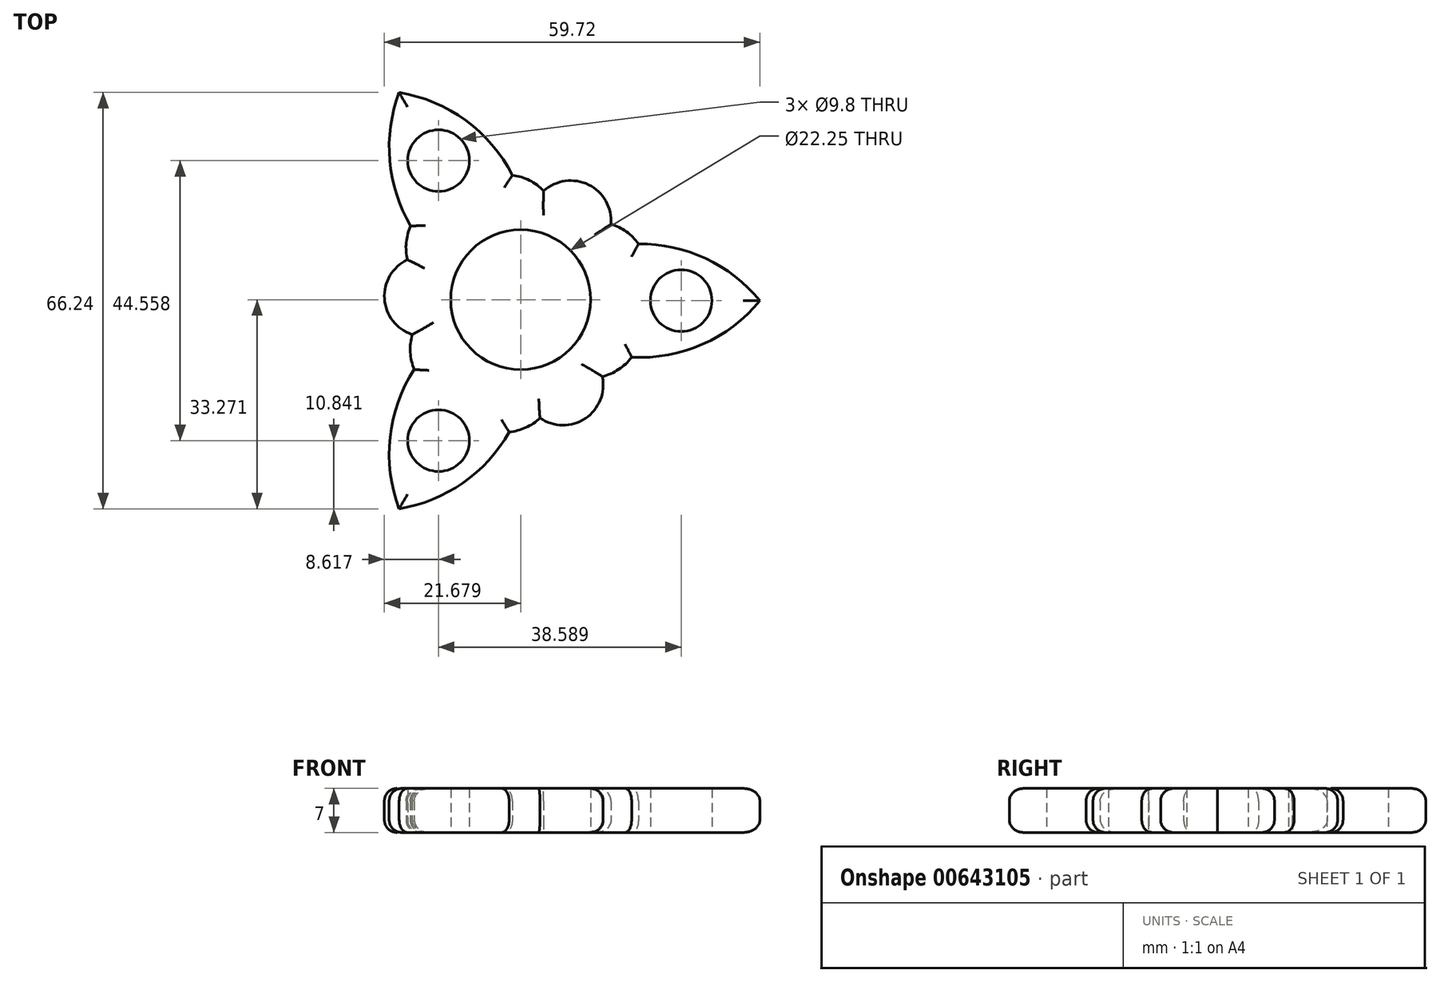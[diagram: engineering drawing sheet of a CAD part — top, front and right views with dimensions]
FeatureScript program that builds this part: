
annotation { "Feature Type Name" : "Feature", "Feature Type Description" : "" }
export const myFeature = defineFeature(function(context is Context, id is Id, definition is map)
    precondition{}
    {
        {
            var Q0;
            Q0=qCreatedBy(makeId("Top.planeOp"),FACE);
            var sketch = newSketch(context, id + "F0", { "sketchPlane" : qUnion([Q0])});
            skCircle(sketch, "E0.2.14", {"center": v(0.2, 0.15) * mm, "radius": 14.78 * mm});
            skCircle(sketch, "E0.2.19", {"center": v(0.2, 0.15) * mm, "radius": 11.12 * mm});
            skPoint(sketch, "E0.center", {"position": v(0, 0) * mm});
            skArc(sketch, "E1", {"start": v(38.24, 0) * mm, "mid": v(24.82, 8.39) * mm, "end": v(9.06, 6.88) * mm});
            skArc(sketch, "E2", {"start": v(18.93, 9.04) * mm, "mid": v(14.55, 12.17) * mm, "end": v(9.17, 11.9) * mm});
            skArc(sketch, "E3.MirrorCS", {"start": v(38.24, 0) * mm, "mid": v(24.82, -8.39) * mm, "end": v(9.06, -6.88) * mm});
            skArc(sketch, "E4.1.3", {"start": v(-1.12, 19.95) * mm, "mid": v(3.85, 17.45) * mm, "end": v(6.07, 12.35) * mm});
            skArc(sketch, "E5.1.0", {"start": v(14.55, 12.17) * mm, "mid": v(11, 18.44) * mm, "end": v(3.85, 17.45) * mm});
            skCircle(sketch, "E6", {"center": v(25.73, 0) * mm, "radius": 4.9 * mm});
            skArc(sketch, "E7.1.0", {"start": v(-17.8, 6.51) * mm, "mid": v(-21.46, 0.3) * mm, "end": v(-17.04, -5.39) * mm});
            skArc(sketch, "E7.1.1", {"start": v(-19.12, 33.12) * mm, "mid": v(-19.67, 17.3) * mm, "end": v(-10.49, 4.4) * mm});
            skArc(sketch, "E7.1.2", {"start": v(-19.12, 33.12) * mm, "mid": v(-5.15, 25.69) * mm, "end": v(1.42, 11.29) * mm});
            skArc(sketch, "E7.1.3", {"start": v(-17.3, 11.87) * mm, "mid": v(-17.8, 6.51) * mm, "end": v(-14.88, 2) * mm});
            skCircle(sketch, "E7.1.4", {"center": v(-12.86, 22.28) * mm, "radius": 4.9 * mm});
            skArc(sketch, "E7.1.5", {"start": v(-16.72, -10.95) * mm, "mid": v(-17.04, -5.39) * mm, "end": v(-13.73, -0.91) * mm});
            skArc(sketch, "E7.2.0", {"start": v(3.26, -18.68) * mm, "mid": v(10.47, -18.74) * mm, "end": v(13.19, -12.06) * mm});
            skArc(sketch, "E7.2.1", {"start": v(-19.12, -33.12) * mm, "mid": v(-5.15, -25.69) * mm, "end": v(1.42, -11.29) * mm});
            skArc(sketch, "E7.2.2", {"start": v(-19.12, -33.12) * mm, "mid": v(-19.67, -17.3) * mm, "end": v(-10.49, -4.4) * mm});
            skArc(sketch, "E7.2.3", {"start": v(-1.63, -20.91) * mm, "mid": v(3.26, -18.68) * mm, "end": v(5.71, -13.89) * mm});
            skCircle(sketch, "E7.2.4", {"center": v(-12.86, -22.28) * mm, "radius": 4.9 * mm});
            skArc(sketch, "E7.2.5", {"start": v(17.84, -9) * mm, "mid": v(13.19, -12.06) * mm, "end": v(7.66, -11.43) * mm});
            skSolve(sketch);
        }
        {
            var Q0;
            {var subQ0=sQuery(id+"F0.wireOp",EDGE,"E2");var subQ4=sQuery(id+"F0.wireOp",EDGE,"E0.2.14");var subQ5=makeQuery(id+"F0.imprint","INTERSECT",VERTEX,{"derivedFrom":[subQ4,subQ0]});Q0=makeQuery(id+"F0.imprint","IMPRINT",FACE,{"disambiguationData":[TD([[makeQuery(id+"F0.imprint","IMPRINT",EDGE,{"disambiguationData":[TD([[subQ5,1.0]])],"derivedFrom":subQ4}),-1.0]])]});}
            var Q1;
            {var subQ0=sQuery(id+"F0.wireOp",EDGE,"E4.1.0");var subQ1=sQuery(id+"F0.wireOp",EDGE,"E0.2.14");var subQ2=makeQuery(id+"F0.imprint","INTERSECT",VERTEX,{"derivedFrom":[subQ1,subQ0]});Q1=makeQuery(id+"F0.imprint","IMPRINT",FACE,{"disambiguationData":[TD([[makeQuery(id+"F0.imprint","IMPRINT",EDGE,{"disambiguationData":[TD([[subQ2,1.0]])],"derivedFrom":subQ1}),-1.0]])]});}
            var Q2;
            Q2=makeQuery(id+"F0.imprint","IMPRINT",FACE,{"disambiguationData":[TD([[makeQuery(id+"F0.imprint","IMPRINT",EDGE,{"derivedFrom":sQuery(id+"F0.wireOp",EDGE,"E0.2.4")}),1.0]])]});
            var Q3;
            {var subQ5=sQuery(id+"F0.wireOp",EDGE,"E5.2.0");Q3=makeQuery(id+"F0.imprint","IMPRINT",FACE,{"disambiguationData":[TD([[makeQuery(id+"F0.imprint","IMPRINT",EDGE,{"derivedFrom":subQ5}),1.0]])]});}
            var Q4;
            {var subQ1=sQuery(id+"F0.wireOp",EDGE,"3faf77e5-a455-4eac-ab54-7ff30253d6db0.MirrorCS");var subQ4=sQuery(id+"F0.wireOp",EDGE,"E0.2.14");var subQ5=makeQuery(id+"F0.imprint","INTERSECT",VERTEX,{"derivedFrom":[subQ4,subQ1]});Q4=makeQuery(id+"F0.imprint","IMPRINT",FACE,{"disambiguationData":[TD([[makeQuery(id+"F0.imprint","IMPRINT",EDGE,{"disambiguationData":[TD([[subQ5,-1.0]])],"derivedFrom":subQ4}),-1.0]])]});}
            var Q5;
            {var subQ0=sQuery(id+"F0.wireOp",EDGE,"E0.2.21");Q5=makeQuery(id+"F0.imprint","IMPRINT",FACE,{"disambiguationData":[TD([[makeQuery(id+"F0.imprint","IMPRINT",EDGE,{"derivedFrom":subQ0}),1.0]])]});}
            var Q6;
            {var subQ0=sQuery(id+"F0.wireOp",EDGE,"E0.1.21");Q6=makeQuery(id+"F0.imprint","IMPRINT",FACE,{"disambiguationData":[TD([[makeQuery(id+"F0.imprint","IMPRINT",EDGE,{"derivedFrom":subQ0}),1.0]])]});}
            var Q7;
            {var subQ0=sQuery(id+"F0.wireOp",EDGE,"E0.2.14");var subQ4=sQuery(id+"F0.wireOp",EDGE,"SB2xlFYN-wPci-y5sM-DaII-UikfFQLFsMd4");var subQ7=makeQuery(id+"F0.imprint","INTERSECT",VERTEX,{"derivedFrom":[subQ4,subQ0]});Q7=makeQuery(id+"F0.imprint","IMPRINT",FACE,{"disambiguationData":[TD([[makeQuery(id+"F0.imprint","IMPRINT",EDGE,{"disambiguationData":[TD([[subQ7,-1.0]])],"derivedFrom":subQ4}),-1.0]])]});}
            var Q8;
            {var subQ5=sQuery(id+"F0.wireOp",EDGE,"E0.1.11");Q8=makeQuery(id+"F0.imprint","IMPRINT",FACE,{"disambiguationData":[TD([[makeQuery(id+"F0.imprint","IMPRINT",EDGE,{"derivedFrom":subQ5}),-1.0]])]});}
            var Q9;
            {var subQ0=sQuery(id+"F0.wireOp",EDGE,"E0.1.17");Q9=makeQuery(id+"F0.imprint","IMPRINT",FACE,{"disambiguationData":[TD([[makeQuery(id+"F0.imprint","IMPRINT",EDGE,{"derivedFrom":subQ0}),-1.0]])]});}
            var Q10;
            {var subQ0=sQuery(id+"F0.wireOp",EDGE,"E0.2.17");Q10=makeQuery(id+"F0.imprint","IMPRINT",FACE,{"disambiguationData":[TD([[makeQuery(id+"F0.imprint","IMPRINT",EDGE,{"derivedFrom":subQ0}),1.0]])]});}
            var Q11;
            {var subQ3=sQuery(id+"F0.wireOp",EDGE,"E4.1.3");var subQ5=sQuery(id+"F0.wireOp",EDGE,"E0.2.14");var subQ6=makeQuery(id+"F0.imprint","INTERSECT",VERTEX,{"derivedFrom":[subQ5,subQ3]});Q11=makeQuery(id+"F0.imprint","IMPRINT",FACE,{"disambiguationData":[TD([[makeQuery(id+"F0.imprint","IMPRINT",EDGE,{"disambiguationData":[TD([[subQ6,-1.0]])],"derivedFrom":subQ5}),-1.0]])]});}
            var Q12;
            {var subQ0=sQuery(id+"F0.wireOp",EDGE,"E0.2.14");var subQ2=sQuery(id+"F0.wireOp",EDGE,"fad0677a-f0d0-457d-b8b5-f5e50509d2e30.MirrorCS");var subQ3=makeQuery(id+"F0.imprint","INTERSECT",VERTEX,{"derivedFrom":[subQ2,subQ0]});Q12=makeQuery(id+"F0.imprint","IMPRINT",FACE,{"disambiguationData":[TD([[makeQuery(id+"F0.imprint","IMPRINT",EDGE,{"disambiguationData":[TD([[subQ3,-1.0]])],"derivedFrom":subQ2}),1.0]])]});}
            var Q13;
            {var subQ5=sQuery(id+"F0.wireOp",EDGE,"E0.2.13");var subQ6=sQuery(id+"F0.wireOp",EDGE,"E0.1.6");var subQ7=makeQuery(id+"F0.imprint","INTERSECT",VERTEX,{"derivedFrom":[subQ6,subQ5]});Q13=makeQuery(id+"F0.imprint","IMPRINT",FACE,{"disambiguationData":[TD([[makeQuery(id+"F0.imprint","IMPRINT",EDGE,{"disambiguationData":[TD([[subQ7,-1.0]])],"derivedFrom":subQ6}),-1.0]])]});}
            var Q14;
            {var subQ0=sQuery(id+"F0.wireOp",EDGE,"adc5b928-cb3e-42c3-bef2-0529e587c3ae.3");Q14=makeQuery(id+"F0.imprint","IMPRINT",FACE,{"disambiguationData":[TD([[makeQuery(id+"F0.imprint","IMPRINT",EDGE,{"derivedFrom":subQ0}),1.0]])]});}
            var Q15;
            {var subQ6=sQuery(id+"F0.wireOp",EDGE,"adc5b928-cb3e-42c3-bef2-0529e587c3ae.0");Q15=makeQuery(id+"F0.imprint","IMPRINT",FACE,{"disambiguationData":[TD([[makeQuery(id+"F0.imprint","IMPRINT",EDGE,{"derivedFrom":subQ6}),1.0]])]});}
            var Q16;
            {var subQ0=sQuery(id+"F0.wireOp",EDGE,"E0.1.11");Q16=makeQuery(id+"F0.imprint","IMPRINT",FACE,{"disambiguationData":[TD([[makeQuery(id+"F0.imprint","IMPRINT",EDGE,{"derivedFrom":subQ0}),1.0]])]});}
            var Q17;
            {var subQ5=sQuery(id+"F0.wireOp",EDGE,"E0.1.13");var subQ6=sQuery(id+"F0.wireOp",EDGE,"UagSYzYK-Bevg-ZJ9g-jcn7-2ZWaxDcqGfQ5");var subQ7=makeQuery(id+"F0.imprint","INTERSECT",VERTEX,{"derivedFrom":[subQ6,subQ5]});Q17=makeQuery(id+"F0.imprint","IMPRINT",FACE,{"disambiguationData":[TD([[makeQuery(id+"F0.imprint","IMPRINT",EDGE,{"disambiguationData":[TD([[subQ7,-1.0]])],"derivedFrom":subQ6}),-1.0]])]});}
            var Q18;
            Q18=makeQuery(id+"F0.imprint","IMPRINT",FACE,{"disambiguationData":[TD([[makeQuery(id+"F0.imprint","IMPRINT",EDGE,{"derivedFrom":sQuery(id+"F0.wireOp",EDGE,"E0.1.4")}),1.0]])]});
            var Q19;
            {var subQ0=sQuery(id+"F0.wireOp",EDGE,"E4.2.0");var subQ1=sQuery(id+"F0.wireOp",EDGE,"E0.2.14");var subQ2=makeQuery(id+"F0.imprint","INTERSECT",VERTEX,{"derivedFrom":[subQ1,subQ0]});Q19=makeQuery(id+"F0.imprint","IMPRINT",FACE,{"disambiguationData":[TD([[makeQuery(id+"F0.imprint","IMPRINT",EDGE,{"disambiguationData":[TD([[subQ2,1.0]])],"derivedFrom":subQ1}),-1.0]])]});}
            var Q20;
            {var subQ5=sQuery(id+"F0.wireOp",EDGE,"E5.1.0");Q20=makeQuery(id+"F0.imprint","IMPRINT",FACE,{"disambiguationData":[TD([[makeQuery(id+"F0.imprint","IMPRINT",EDGE,{"derivedFrom":subQ5}),1.0]])]});}
            var Q21;
            {var subQ1=sQuery(id+"F0.wireOp",EDGE,"2409a4e0-c98d-46af-a0ef-b846dedd611c0.MirrorCS");var subQ5=sQuery(id+"F0.wireOp",EDGE,"UagSYzYK-Bevg-ZJ9g-jcn7-2ZWaxDcqGfQ5");var subQ8=makeQuery(id+"F0.imprint","INTERSECT",VERTEX,{"derivedFrom":[subQ5,subQ1]});Q21=makeQuery(id+"F0.imprint","IMPRINT",FACE,{"disambiguationData":[TD([[makeQuery(id+"F0.imprint","IMPRINT",EDGE,{"disambiguationData":[TD([[subQ8,-1.0]])],"derivedFrom":subQ5}),1.0]])]});}
            var Q22;
            {var subQ0=sQuery(id+"F0.wireOp",EDGE,"E0.2.17");Q22=makeQuery(id+"F0.imprint","IMPRINT",FACE,{"disambiguationData":[TD([[makeQuery(id+"F0.imprint","IMPRINT",EDGE,{"derivedFrom":subQ0}),-1.0]])]});}
            var Q23;
            {var subQ0=sQuery(id+"F0.wireOp",EDGE,"E4.2.3");var subQ6=sQuery(id+"F0.wireOp",EDGE,"E0.2.14");var subQ8=makeQuery(id+"F0.imprint","INTERSECT",VERTEX,{"derivedFrom":[subQ6,subQ0]});Q23=makeQuery(id+"F0.imprint","IMPRINT",FACE,{"disambiguationData":[TD([[makeQuery(id+"F0.imprint","IMPRINT",EDGE,{"disambiguationData":[TD([[subQ8,-1.0]])],"derivedFrom":subQ6}),-1.0]])]});}
            var Q24;
            {var subQ2=sQuery(id+"F0.wireOp",EDGE,"edb74509-46f7-4ae7-9a82-a3f9e29243620.MirrorCS");Q24=makeQuery(id+"F0.imprint","IMPRINT",FACE,{"disambiguationData":[TD([[makeQuery(id+"F0.imprint","IMPRINT",EDGE,{"derivedFrom":subQ2}),1.0]])]});}
            var Q25;
            {var subQ0=sQuery(id+"F0.wireOp",EDGE,"E0.2.14");var subQ4=sQuery(id+"F0.wireOp",EDGE,"E0.1.18");var subQ7=makeQuery(id+"F0.imprint","INTERSECT",VERTEX,{"derivedFrom":[subQ4,subQ0]});Q25=makeQuery(id+"F0.imprint","IMPRINT",FACE,{"disambiguationData":[TD([[makeQuery(id+"F0.imprint","IMPRINT",EDGE,{"disambiguationData":[TD([[subQ7,-1.0]])],"derivedFrom":subQ4}),-1.0]])]});}
            var Q26;
            {var subQ5=sQuery(id+"F0.wireOp",EDGE,"E0.2.6");var subQ6=sQuery(id+"F0.wireOp",EDGE,"fad0677a-f0d0-457d-b8b5-f5e50509d2e30.MirrorCS");var subQ7=makeQuery(id+"F0.imprint","INTERSECT",VERTEX,{"derivedFrom":[subQ6,subQ5]});Q26=makeQuery(id+"F0.imprint","IMPRINT",FACE,{"disambiguationData":[TD([[makeQuery(id+"F0.imprint","IMPRINT",EDGE,{"disambiguationData":[TD([[subQ7,-1.0]])],"derivedFrom":subQ5}),-1.0]])]});}
            var Q27;
            {var subQ0=sQuery(id+"F0.wireOp",EDGE,"E0.1.17");Q27=makeQuery(id+"F0.imprint","IMPRINT",FACE,{"disambiguationData":[TD([[makeQuery(id+"F0.imprint","IMPRINT",EDGE,{"derivedFrom":subQ0}),1.0]])]});}
            var Q28;
            {var subQ2=sQuery(id+"F0.wireOp",EDGE,"E0.2.11");Q28=makeQuery(id+"F0.imprint","IMPRINT",FACE,{"disambiguationData":[TD([[makeQuery(id+"F0.imprint","IMPRINT",EDGE,{"derivedFrom":subQ2}),-1.0]])]});}
            var Q29;
            {var subQ5=sQuery(id+"F0.wireOp",EDGE,"C1GWnhyf-GRCL-3z4E-Whwz-ZzzRUctmxLWt");Q29=makeQuery(id+"F0.imprint","IMPRINT",FACE,{"disambiguationData":[TD([[makeQuery(id+"F0.imprint","IMPRINT",EDGE,{"derivedFrom":subQ5}),1.0]])]});}
            var Q30;
            {var subQ0=sQuery(id+"F0.wireOp",EDGE,"E0.1.10");var subQ1=sQuery(id+"F0.wireOp",EDGE,"E0.1.1");var subQ3=makeQuery(id+"F0.imprint","INTERSECT",VERTEX,{"derivedFrom":[subQ1,subQ0]});Q30=makeQuery(id+"F0.imprint","IMPRINT",FACE,{"disambiguationData":[TD([[makeQuery(id+"F0.imprint","IMPRINT",EDGE,{"disambiguationData":[TD([[subQ3,1.0]])],"derivedFrom":subQ1}),1.0]])]});}
            var Q31;
            {var subQ0=sQuery(id+"F0.wireOp",EDGE,"E0.1.8");Q31=makeQuery(id+"F0.imprint","IMPRINT",FACE,{"disambiguationData":[TD([[makeQuery(id+"F0.imprint","IMPRINT",EDGE,{"derivedFrom":subQ0}),1.0]])]});}
            var Q32;
            {var subQ0=sQuery(id+"F0.wireOp",EDGE,"E0.2.10");var subQ1=sQuery(id+"F0.wireOp",EDGE,"E0.1.6");var subQ2=makeQuery(id+"F0.imprint","INTERSECT",VERTEX,{"derivedFrom":[subQ1,subQ0]});Q32=makeQuery(id+"F0.imprint","IMPRINT",FACE,{"disambiguationData":[TD([[makeQuery(id+"F0.imprint","IMPRINT",EDGE,{"disambiguationData":[TD([[subQ2,-1.0]])],"derivedFrom":subQ1}),-1.0]])]});}
            var Q33;
            {var subQ0=sQuery(id+"F0.wireOp",EDGE,"2409a4e0-c98d-46af-a0ef-b846dedd611c0.MirrorCS");var subQ1=sQuery(id+"F0.wireOp",EDGE,"UagSYzYK-Bevg-ZJ9g-jcn7-2ZWaxDcqGfQ5");var subQ3=makeQuery(id+"F0.imprint","INTERSECT",VERTEX,{"derivedFrom":[subQ1,subQ0]});Q33=makeQuery(id+"F0.imprint","IMPRINT",FACE,{"disambiguationData":[TD([[makeQuery(id+"F0.imprint","IMPRINT",EDGE,{"disambiguationData":[TD([[subQ3,1.0]])],"derivedFrom":subQ1}),1.0]])]});}
            var Q34;
            {var subQ0=sQuery(id+"F0.wireOp",EDGE,"edb74509-46f7-4ae7-9a82-a3f9e29243620.MirrorCS");Q34=makeQuery(id+"F0.imprint","IMPRINT",FACE,{"disambiguationData":[TD([[makeQuery(id+"F0.imprint","IMPRINT",EDGE,{"derivedFrom":subQ0}),-1.0]])]});}
            var Q35;
            {var subQ0=sQuery(id+"F0.wireOp",EDGE,"E0.1.9");Q35=makeQuery(id+"F0.imprint","IMPRINT",FACE,{"disambiguationData":[TD([[makeQuery(id+"F0.imprint","IMPRINT",EDGE,{"derivedFrom":subQ0}),1.0]])]});}
            var Q36;
            {var subQ0=sQuery(id+"F0.wireOp",EDGE,"E0.2.6");var subQ1=sQuery(id+"F0.wireOp",EDGE,"8629fafa-8f78-4977-a6de-91e64b7f8d9b0.MirrorCS");var subQ2=makeQuery(id+"F0.imprint","INTERSECT",VERTEX,{"derivedFrom":[subQ1,subQ0]});Q36=makeQuery(id+"F0.imprint","IMPRINT",FACE,{"disambiguationData":[TD([[makeQuery(id+"F0.imprint","IMPRINT",EDGE,{"disambiguationData":[TD([[subQ2,-1.0]])],"derivedFrom":subQ1}),-1.0]])]});}
            var Q37;
            {var subQ0=sQuery(id+"F0.wireOp",EDGE,"E0.2.12");var subQ1=sQuery(id+"F0.wireOp",EDGE,"E0.2.6");var subQ3=makeQuery(id+"F0.imprint","INTERSECT",VERTEX,{"derivedFrom":[subQ1,subQ0]});Q37=makeQuery(id+"F0.imprint","IMPRINT",FACE,{"disambiguationData":[TD([[makeQuery(id+"F0.imprint","IMPRINT",EDGE,{"disambiguationData":[TD([[subQ3,1.0]])],"derivedFrom":subQ1}),1.0]])]});}
            var Q38;
            {var subQ0=sQuery(id+"F0.wireOp",EDGE,"E0.1.12");var subQ1=sQuery(id+"F0.wireOp",EDGE,"E0.1.6");var subQ3=makeQuery(id+"F0.imprint","INTERSECT",VERTEX,{"derivedFrom":[subQ1,subQ0]});Q38=makeQuery(id+"F0.imprint","IMPRINT",FACE,{"disambiguationData":[TD([[makeQuery(id+"F0.imprint","IMPRINT",EDGE,{"disambiguationData":[TD([[subQ3,1.0]])],"derivedFrom":subQ1}),1.0]])]});}
            var Q39;
            {var subQ0=sQuery(id+"F0.wireOp",EDGE,"X4Hcboga-jWI0-KNgK-RObT-s1H3nTZ6lbSe");var subQ1=sQuery(id+"F0.wireOp",EDGE,"8629fafa-8f78-4977-a6de-91e64b7f8d9b0.MirrorCS");var subQ3=makeQuery(id+"F0.imprint","INTERSECT",VERTEX,{"derivedFrom":[subQ1,subQ0]});Q39=makeQuery(id+"F0.imprint","IMPRINT",FACE,{"disambiguationData":[TD([[makeQuery(id+"F0.imprint","IMPRINT",EDGE,{"disambiguationData":[TD([[subQ3,1.0]])],"derivedFrom":subQ1}),-1.0]])]});}
            var Q40;
            {var subQ0=sQuery(id+"F0.wireOp",EDGE,"E0.2.8");Q40=makeQuery(id+"F0.imprint","IMPRINT",FACE,{"disambiguationData":[TD([[makeQuery(id+"F0.imprint","IMPRINT",EDGE,{"derivedFrom":subQ0}),1.0]])]});}
            var Q41;
            {var subQ0=sQuery(id+"F0.wireOp",EDGE,"E0.2.6");var subQ1=sQuery(id+"F0.wireOp",EDGE,"8629fafa-8f78-4977-a6de-91e64b7f8d9b0.MirrorCS");var subQ2=makeQuery(id+"F0.imprint","INTERSECT",VERTEX,{"derivedFrom":[subQ1,subQ0]});Q41=makeQuery(id+"F0.imprint","IMPRINT",FACE,{"disambiguationData":[TD([[makeQuery(id+"F0.imprint","IMPRINT",EDGE,{"disambiguationData":[TD([[subQ2,-1.0]])],"derivedFrom":subQ1}),1.0]])]});}
            var Q42;
            {var subQ0=sQuery(id+"F0.wireOp",EDGE,"E0.1.10");var subQ1=sQuery(id+"F0.wireOp",EDGE,"UagSYzYK-Bevg-ZJ9g-jcn7-2ZWaxDcqGfQ5");var subQ2=makeQuery(id+"F0.imprint","INTERSECT",VERTEX,{"derivedFrom":[subQ1,subQ0]});Q42=makeQuery(id+"F0.imprint","IMPRINT",FACE,{"disambiguationData":[TD([[makeQuery(id+"F0.imprint","IMPRINT",EDGE,{"disambiguationData":[TD([[subQ2,-1.0]])],"derivedFrom":subQ1}),1.0]])]});}
            var Q43;
            {var subQ0=sQuery(id+"F0.wireOp",EDGE,"nV3mjgLP-5YSs-PFaL-RFMX-QoyXoHo6brJm");Q43=makeQuery(id+"F0.imprint","IMPRINT",FACE,{"disambiguationData":[TD([[makeQuery(id+"F0.imprint","IMPRINT",EDGE,{"derivedFrom":subQ0}),1.0]])]});}
            var Q44;
            {var subQ0=sQuery(id+"F0.wireOp",EDGE,"E0.1.13");var subQ1=sQuery(id+"F0.wireOp",EDGE,"UagSYzYK-Bevg-ZJ9g-jcn7-2ZWaxDcqGfQ5");var subQ2=makeQuery(id+"F0.imprint","INTERSECT",VERTEX,{"derivedFrom":[subQ1,subQ0]});Q44=makeQuery(id+"F0.imprint","IMPRINT",FACE,{"disambiguationData":[TD([[makeQuery(id+"F0.imprint","IMPRINT",EDGE,{"disambiguationData":[TD([[subQ2,-1.0]])],"derivedFrom":subQ1}),1.0]])]});}
            var Q45;
            {var subQ0=sQuery(id+"F0.wireOp",EDGE,"E0.1.10");var subQ1=sQuery(id+"F0.wireOp",EDGE,"UagSYzYK-Bevg-ZJ9g-jcn7-2ZWaxDcqGfQ5");var subQ2=makeQuery(id+"F0.imprint","INTERSECT",VERTEX,{"derivedFrom":[subQ1,subQ0]});Q45=makeQuery(id+"F0.imprint","IMPRINT",FACE,{"disambiguationData":[TD([[makeQuery(id+"F0.imprint","IMPRINT",EDGE,{"disambiguationData":[TD([[subQ2,-1.0]])],"derivedFrom":subQ1}),-1.0]])]});}
            var Q46;
            {var subQ0=sQuery(id+"F0.wireOp",EDGE,"E0.2.19");var subQ1=sQuery(id+"F0.wireOp",EDGE,"E0.1.6");var subQ2=makeQuery(id+"F0.imprint","INTERSECT",VERTEX,{"derivedFrom":[subQ1,subQ0]});Q46=makeQuery(id+"F0.imprint","IMPRINT",FACE,{"disambiguationData":[TD([[makeQuery(id+"F0.imprint","IMPRINT",EDGE,{"disambiguationData":[TD([[subQ2,-1.0]])],"derivedFrom":subQ1}),1.0]])]});}
            var Q47;
            {var subQ0=sQuery(id+"F0.wireOp",EDGE,"E0.2.13");var subQ1=sQuery(id+"F0.wireOp",EDGE,"E0.1.18");var subQ2=makeQuery(id+"F0.imprint","INTERSECT",VERTEX,{"derivedFrom":[subQ1,subQ0]});Q47=makeQuery(id+"F0.imprint","IMPRINT",FACE,{"disambiguationData":[TD([[makeQuery(id+"F0.imprint","IMPRINT",EDGE,{"disambiguationData":[TD([[subQ2,-1.0]])],"derivedFrom":subQ1}),-1.0]])]});}
            var Q48;
            {var subQ0=sQuery(id+"F0.wireOp",EDGE,"E0.1.13");var subQ1=sQuery(id+"F0.wireOp",EDGE,"SB2xlFYN-wPci-y5sM-DaII-UikfFQLFsMd4");var subQ2=makeQuery(id+"F0.imprint","INTERSECT",VERTEX,{"derivedFrom":[subQ1,subQ0]});Q48=makeQuery(id+"F0.imprint","IMPRINT",FACE,{"disambiguationData":[TD([[makeQuery(id+"F0.imprint","IMPRINT",EDGE,{"disambiguationData":[TD([[subQ2,-1.0]])],"derivedFrom":subQ1}),-1.0]])]});}
            var Q49;
            {var subQ0=sQuery(id+"F0.wireOp",EDGE,"E0.2.9");Q49=makeQuery(id+"F0.imprint","IMPRINT",FACE,{"disambiguationData":[TD([[makeQuery(id+"F0.imprint","IMPRINT",EDGE,{"derivedFrom":subQ0}),1.0]])]});}
            var Q50;
            {var subQ0=sQuery(id+"F0.wireOp",EDGE,"mW2aMCEq-i75T-0uT7-j5cR-gpWakHIjF3lY");var subQ1=makeQuery(id+"F0.imprint","INTERSECT",VERTEX,{"derivedFrom":[sQuery(id+"F0.wireOp",EDGE,"adc5b928-cb3e-42c3-bef2-0529e587c3ae.3"),subQ0]});Q50=makeQuery(id+"F0.imprint","IMPRINT",FACE,{"disambiguationData":[TD([[makeQuery(id+"F0.imprint","IMPRINT",EDGE,{"disambiguationData":[TD([[subQ1,1.0]])],"derivedFrom":subQ0}),1.0]])]});}
            var Q51;
            {var subQ0=sQuery(id+"F0.wireOp",EDGE,"E0.2.18");var subQ1=sQuery(id+"F0.wireOp",EDGE,"fad0677a-f0d0-457d-b8b5-f5e50509d2e30.MirrorCS");var subQ2=makeQuery(id+"F0.imprint","INTERSECT",VERTEX,{"derivedFrom":[subQ1,subQ0]});Q51=makeQuery(id+"F0.imprint","IMPRINT",FACE,{"disambiguationData":[TD([[makeQuery(id+"F0.imprint","IMPRINT",EDGE,{"disambiguationData":[TD([[subQ2,-1.0]])],"derivedFrom":subQ1}),1.0]])]});}
            var Q52;
            {var subQ0=sQuery(id+"F0.wireOp",EDGE,"E0.2.19");var subQ1=sQuery(id+"F0.wireOp",EDGE,"8629fafa-8f78-4977-a6de-91e64b7f8d9b0.MirrorCS");var subQ2=makeQuery(id+"F0.imprint","INTERSECT",VERTEX,{"derivedFrom":[subQ1,subQ0]});Q52=makeQuery(id+"F0.imprint","IMPRINT",FACE,{"disambiguationData":[TD([[makeQuery(id+"F0.imprint","IMPRINT",EDGE,{"disambiguationData":[TD([[subQ2,-1.0]])],"derivedFrom":subQ1}),-1.0]])]});}
            var Q53;
            {var subQ0=sQuery(id+"F0.wireOp",EDGE,"E0.2.19");var subQ1=sQuery(id+"F0.wireOp",EDGE,"8629fafa-8f78-4977-a6de-91e64b7f8d9b0.MirrorCS");var subQ2=makeQuery(id+"F0.imprint","INTERSECT",VERTEX,{"derivedFrom":[subQ1,subQ0]});Q53=makeQuery(id+"F0.imprint","IMPRINT",FACE,{"disambiguationData":[TD([[makeQuery(id+"F0.imprint","IMPRINT",EDGE,{"disambiguationData":[TD([[subQ2,-1.0]])],"derivedFrom":subQ1}),1.0]])]});}
            var Q54;
            {var subQ0=sQuery(id+"F0.wireOp",EDGE,"E0.2.10");var subQ1=sQuery(id+"F0.wireOp",EDGE,"E0.2.1");var subQ3=makeQuery(id+"F0.imprint","INTERSECT",VERTEX,{"derivedFrom":[subQ1,subQ0]});Q54=makeQuery(id+"F0.imprint","IMPRINT",FACE,{"disambiguationData":[TD([[makeQuery(id+"F0.imprint","IMPRINT",EDGE,{"disambiguationData":[TD([[subQ3,1.0]])],"derivedFrom":subQ1}),1.0]])]});}
            var Q55;
            {var subQ0=sQuery(id+"F0.wireOp",EDGE,"E0.2.18");var subQ1=sQuery(id+"F0.wireOp",EDGE,"8629fafa-8f78-4977-a6de-91e64b7f8d9b0.MirrorCS");var subQ2=makeQuery(id+"F0.imprint","INTERSECT",VERTEX,{"derivedFrom":[subQ1,subQ0]});Q55=makeQuery(id+"F0.imprint","IMPRINT",FACE,{"disambiguationData":[TD([[makeQuery(id+"F0.imprint","IMPRINT",EDGE,{"disambiguationData":[TD([[subQ2,-1.0]])],"derivedFrom":subQ1}),-1.0]])]});}
            var Q56;
            {var subQ0=sQuery(id+"F0.wireOp",EDGE,"E0.2.13");var subQ1=sQuery(id+"F0.wireOp",EDGE,"E0.1.6");var subQ2=makeQuery(id+"F0.imprint","INTERSECT",VERTEX,{"derivedFrom":[subQ1,subQ0]});Q56=makeQuery(id+"F0.imprint","IMPRINT",FACE,{"disambiguationData":[TD([[makeQuery(id+"F0.imprint","IMPRINT",EDGE,{"disambiguationData":[TD([[subQ2,-1.0]])],"derivedFrom":subQ1}),1.0]])]});}
            var Q57;
            {var subQ0=sQuery(id+"F0.wireOp",EDGE,"E0.2.19");var subQ1=sQuery(id+"F0.wireOp",EDGE,"UagSYzYK-Bevg-ZJ9g-jcn7-2ZWaxDcqGfQ5");var subQ2=makeQuery(id+"F0.imprint","INTERSECT",VERTEX,{"derivedFrom":[subQ1,subQ0]});Q57=makeQuery(id+"F0.imprint","IMPRINT",FACE,{"disambiguationData":[TD([[makeQuery(id+"F0.imprint","IMPRINT",EDGE,{"disambiguationData":[TD([[subQ2,-1.0]])],"derivedFrom":subQ1}),1.0]])]});}
            var Q58;
            {var subQ0=sQuery(id+"F0.wireOp",EDGE,"E0.2.19");var subQ1=sQuery(id+"F0.wireOp",EDGE,"E0.1.6");var subQ2=makeQuery(id+"F0.imprint","INTERSECT",VERTEX,{"derivedFrom":[subQ1,subQ0]});Q58=makeQuery(id+"F0.imprint","IMPRINT",FACE,{"disambiguationData":[TD([[makeQuery(id+"F0.imprint","IMPRINT",EDGE,{"disambiguationData":[TD([[subQ2,-1.0]])],"derivedFrom":subQ1}),-1.0]])]});}
            var Q59;
            {var subQ0=sQuery(id+"F0.wireOp",EDGE,"E0.2.11");Q59=makeQuery(id+"F0.imprint","IMPRINT",FACE,{"disambiguationData":[TD([[makeQuery(id+"F0.imprint","IMPRINT",EDGE,{"derivedFrom":subQ0}),1.0]])]});}
            var Q60;
            {var subQ0=sQuery(id+"F0.wireOp",EDGE,"E0.2.19");var subQ1=sQuery(id+"F0.wireOp",EDGE,"UagSYzYK-Bevg-ZJ9g-jcn7-2ZWaxDcqGfQ5");var subQ2=makeQuery(id+"F0.imprint","INTERSECT",VERTEX,{"derivedFrom":[subQ1,subQ0]});Q60=makeQuery(id+"F0.imprint","IMPRINT",FACE,{"disambiguationData":[TD([[makeQuery(id+"F0.imprint","IMPRINT",EDGE,{"disambiguationData":[TD([[subQ2,-1.0]])],"derivedFrom":subQ1}),-1.0]])]});}
            var Q61;
            {var subQ0=sQuery(id+"F0.wireOp",EDGE,"E0.2.10");var subQ1=sQuery(id+"F0.wireOp",EDGE,"E0.1.6");var subQ2=makeQuery(id+"F0.imprint","INTERSECT",VERTEX,{"derivedFrom":[subQ1,subQ0]});Q61=makeQuery(id+"F0.imprint","IMPRINT",FACE,{"disambiguationData":[TD([[makeQuery(id+"F0.imprint","IMPRINT",EDGE,{"disambiguationData":[TD([[subQ2,-1.0]])],"derivedFrom":subQ1}),1.0]])]});}
            var Q62;
            {var subQ0=sQuery(id+"F0.wireOp",EDGE,"E0.2.19");var subQ1=sQuery(id+"F0.wireOp",EDGE,"E0.2.10");var subQ3=makeQuery(id+"F0.imprint","INTERSECT",VERTEX,{"derivedFrom":[subQ1,subQ0]});Q62=makeQuery(id+"F0.imprint","IMPRINT",FACE,{"disambiguationData":[TD([[makeQuery(id+"F0.imprint","IMPRINT",EDGE,{"disambiguationData":[TD([[subQ3,1.0]])],"derivedFrom":subQ1}),-1.0]])]});}
            var Q63;
            {var subQ1=sQuery(id+"F0.wireOp",EDGE,"UagSYzYK-Bevg-ZJ9g-jcn7-2ZWaxDcqGfQ5");var subQ3=sQuery(id+"F0.wireOp",EDGE,"E0.2.14");var subQ4=makeQuery(id+"F0.imprint","INTERSECT",VERTEX,{"derivedFrom":[subQ1,subQ3]});Q63=makeQuery(id+"F0.imprint","IMPRINT",FACE,{"disambiguationData":[TD([[makeQuery(id+"F0.imprint","IMPRINT",EDGE,{"disambiguationData":[TD([[subQ4,-1.0]])],"derivedFrom":subQ3}),-1.0]])]});}
            var Q64;
            {var subQ1=sQuery(id+"F0.wireOp",EDGE,"E0.1.10");var subQ3=sQuery(id+"F0.wireOp",EDGE,"E0.2.14");var subQ4=makeQuery(id+"F0.imprint","INTERSECT",VERTEX,{"derivedFrom":[subQ1,subQ3]});Q64=makeQuery(id+"F0.imprint","IMPRINT",FACE,{"disambiguationData":[TD([[makeQuery(id+"F0.imprint","IMPRINT",EDGE,{"disambiguationData":[TD([[subQ4,1.0]])],"derivedFrom":subQ3}),-1.0]])]});}
            var Q65;
            {var subQ0=sQuery(id+"F0.wireOp",EDGE,"E0.2.19");var subQ1=sQuery(id+"F0.wireOp",EDGE,"8629fafa-8f78-4977-a6de-91e64b7f8d9b0.MirrorCS");var subQ3=makeQuery(id+"F0.imprint","INTERSECT",VERTEX,{"derivedFrom":[subQ1,subQ0]});Q65=makeQuery(id+"F0.imprint","IMPRINT",FACE,{"disambiguationData":[TD([[makeQuery(id+"F0.imprint","IMPRINT",EDGE,{"disambiguationData":[TD([[subQ3,1.0]])],"derivedFrom":subQ1}),-1.0]])]});}
            var Q66;
            {var subQ0=sQuery(id+"F0.wireOp",EDGE,"E0.2.19");var subQ1=sQuery(id+"F0.wireOp",EDGE,"E0.1.6");var subQ3=makeQuery(id+"F0.imprint","INTERSECT",VERTEX,{"derivedFrom":[subQ1,subQ0]});Q66=makeQuery(id+"F0.imprint","IMPRINT",FACE,{"disambiguationData":[TD([[makeQuery(id+"F0.imprint","IMPRINT",EDGE,{"disambiguationData":[TD([[subQ3,1.0]])],"derivedFrom":subQ1}),1.0]])]});}
            var Q67;
            {var subQ0=sQuery(id+"F0.wireOp",EDGE,"E0.2.19");var subQ1=sQuery(id+"F0.wireOp",EDGE,"UagSYzYK-Bevg-ZJ9g-jcn7-2ZWaxDcqGfQ5");var subQ3=makeQuery(id+"F0.imprint","INTERSECT",VERTEX,{"derivedFrom":[subQ1,subQ0]});Q67=makeQuery(id+"F0.imprint","IMPRINT",FACE,{"disambiguationData":[TD([[makeQuery(id+"F0.imprint","IMPRINT",EDGE,{"disambiguationData":[TD([[subQ3,1.0]])],"derivedFrom":subQ1}),1.0]])]});}
            var Q68;
            {var subQ0=sQuery(id+"F0.wireOp",EDGE,"E0.2.19");var subQ1=sQuery(id+"F0.wireOp",EDGE,"E0.2.6");var subQ3=makeQuery(id+"F0.imprint","INTERSECT",VERTEX,{"derivedFrom":[subQ1,subQ0]});Q68=makeQuery(id+"F0.imprint","IMPRINT",FACE,{"disambiguationData":[TD([[makeQuery(id+"F0.imprint","IMPRINT",EDGE,{"disambiguationData":[TD([[subQ3,1.0]])],"derivedFrom":subQ1}),1.0]])]});}
            var Q69;
            {var subQ1=sQuery(id+"F0.wireOp",EDGE,"8629fafa-8f78-4977-a6de-91e64b7f8d9b0.MirrorCS");var subQ3=sQuery(id+"F0.wireOp",EDGE,"E0.2.14");var subQ4=makeQuery(id+"F0.imprint","INTERSECT",VERTEX,{"derivedFrom":[subQ1,subQ3]});Q69=makeQuery(id+"F0.imprint","IMPRINT",FACE,{"disambiguationData":[TD([[makeQuery(id+"F0.imprint","IMPRINT",EDGE,{"disambiguationData":[TD([[subQ4,1.0]])],"derivedFrom":subQ3}),-1.0]])]});}
            var Q70;
            {var subQ1=sQuery(id+"F0.wireOp",EDGE,"E0.2.10");var subQ3=sQuery(id+"F0.wireOp",EDGE,"E0.2.14");var subQ4=makeQuery(id+"F0.imprint","INTERSECT",VERTEX,{"derivedFrom":[subQ1,subQ3]});Q70=makeQuery(id+"F0.imprint","IMPRINT",FACE,{"disambiguationData":[TD([[makeQuery(id+"F0.imprint","IMPRINT",EDGE,{"disambiguationData":[TD([[subQ4,1.0]])],"derivedFrom":subQ3}),-1.0]])]});}
            var Q71;
            {var subQ1=sQuery(id+"F0.wireOp",EDGE,"E0.1.6");var subQ3=sQuery(id+"F0.wireOp",EDGE,"E0.2.14");var subQ4=makeQuery(id+"F0.imprint","INTERSECT",VERTEX,{"derivedFrom":[subQ1,subQ3]});Q71=makeQuery(id+"F0.imprint","IMPRINT",FACE,{"disambiguationData":[TD([[makeQuery(id+"F0.imprint","IMPRINT",EDGE,{"disambiguationData":[TD([[subQ4,-1.0]])],"derivedFrom":subQ3}),-1.0]])]});}
            var Q72;
            {var subQ0=sQuery(id+"F0.wireOp",EDGE,"E0.2.19");var subQ1=sQuery(id+"F0.wireOp",EDGE,"E0.1.10");var subQ3=makeQuery(id+"F0.imprint","INTERSECT",VERTEX,{"derivedFrom":[subQ1,subQ0]});Q72=makeQuery(id+"F0.imprint","IMPRINT",FACE,{"disambiguationData":[TD([[makeQuery(id+"F0.imprint","IMPRINT",EDGE,{"disambiguationData":[TD([[subQ3,1.0]])],"derivedFrom":subQ1}),-1.0]])]});}
            var Q73;
            {var subQ0=sQuery(id+"F0.wireOp",EDGE,"E0.1.10");var subQ1=sQuery(id+"F0.wireOp",EDGE,"E0.1.1");var subQ2=makeQuery(id+"F0.imprint","INTERSECT",VERTEX,{"derivedFrom":[subQ1,subQ0]});Q73=makeQuery(id+"F0.imprint","IMPRINT",FACE,{"disambiguationData":[TD([[makeQuery(id+"F0.imprint","IMPRINT",EDGE,{"disambiguationData":[TD([[subQ2,-1.0]])],"derivedFrom":subQ1}),-1.0]])]});}
            var Q74;
            {var subQ1=sQuery(id+"F0.wireOp",EDGE,"adc5b928-cb3e-42c3-bef2-0529e587c3ae.1");var subQ3=sQuery(id+"F0.wireOp",EDGE,"2409a4e0-c98d-46af-a0ef-b846dedd611c0.MirrorCS");var subQ4=makeQuery(id+"F0.imprint","INTERSECT",VERTEX,{"derivedFrom":[subQ1,subQ3]});Q74=makeQuery(id+"F0.imprint","IMPRINT",FACE,{"disambiguationData":[TD([[makeQuery(id+"F0.imprint","IMPRINT",EDGE,{"disambiguationData":[TD([[subQ4,1.0]])],"derivedFrom":subQ3}),1.0]])]});}
            var Q75;
            {var subQ1=sQuery(id+"F0.wireOp",EDGE,"E0.2.6");var subQ3=sQuery(id+"F0.wireOp",EDGE,"E0.2.14");var subQ4=makeQuery(id+"F0.imprint","INTERSECT",VERTEX,{"derivedFrom":[subQ1,subQ3]});Q75=makeQuery(id+"F0.imprint","IMPRINT",FACE,{"disambiguationData":[TD([[makeQuery(id+"F0.imprint","IMPRINT",EDGE,{"disambiguationData":[TD([[subQ4,-1.0]])],"derivedFrom":subQ3}),-1.0]])]});}
            var Q76;
            {var subQ0=sQuery(id+"F0.wireOp",EDGE,"E0.1.7");var subQ1=sQuery(id+"F0.wireOp",EDGE,"E0.1.1");var subQ2=makeQuery(id+"F0.imprint","INTERSECT",VERTEX,{"derivedFrom":[subQ1,subQ0]});Q76=makeQuery(id+"F0.imprint","IMPRINT",FACE,{"disambiguationData":[TD([[makeQuery(id+"F0.imprint","IMPRINT",EDGE,{"disambiguationData":[TD([[subQ2,-1.0]])],"derivedFrom":subQ1}),-1.0]])]});}
            var Q77;
            {var subQ1=sQuery(id+"F0.wireOp",EDGE,"adc5b928-cb3e-42c3-bef2-0529e587c3ae.1");var subQ3=sQuery(id+"F0.wireOp",EDGE,"2409a4e0-c98d-46af-a0ef-b846dedd611c0.MirrorCS");var subQ4=makeQuery(id+"F0.imprint","INTERSECT",VERTEX,{"derivedFrom":[subQ1,subQ3]});Q77=makeQuery(id+"F0.imprint","IMPRINT",FACE,{"disambiguationData":[TD([[makeQuery(id+"F0.imprint","IMPRINT",EDGE,{"disambiguationData":[TD([[subQ4,-1.0]])],"derivedFrom":subQ3}),1.0]])]});}
            var Q78;
            {var subQ0=sQuery(id+"F0.wireOp",EDGE,"E0.2.7");var subQ1=sQuery(id+"F0.wireOp",EDGE,"E0.2.1");var subQ2=makeQuery(id+"F0.imprint","INTERSECT",VERTEX,{"derivedFrom":[subQ1,subQ0]});Q78=makeQuery(id+"F0.imprint","IMPRINT",FACE,{"disambiguationData":[TD([[makeQuery(id+"F0.imprint","IMPRINT",EDGE,{"disambiguationData":[TD([[subQ2,-1.0]])],"derivedFrom":subQ1}),-1.0]])]});}
            var Q79;
            {var subQ1=sQuery(id+"F0.wireOp",EDGE,"adc5b928-cb3e-42c3-bef2-0529e587c3ae.4");var subQ3=sQuery(id+"F0.wireOp",EDGE,"X4Hcboga-jWI0-KNgK-RObT-s1H3nTZ6lbSe");var subQ4=makeQuery(id+"F0.imprint","INTERSECT",VERTEX,{"derivedFrom":[subQ1,subQ3]});Q79=makeQuery(id+"F0.imprint","IMPRINT",FACE,{"disambiguationData":[TD([[makeQuery(id+"F0.imprint","IMPRINT",EDGE,{"disambiguationData":[TD([[subQ4,1.0]])],"derivedFrom":subQ3}),-1.0]])]});}
            var Q80;
            {var subQ1=sQuery(id+"F0.wireOp",EDGE,"adc5b928-cb3e-42c3-bef2-0529e587c3ae.5");var subQ3=sQuery(id+"F0.wireOp",EDGE,"X4Hcboga-jWI0-KNgK-RObT-s1H3nTZ6lbSe");var subQ4=makeQuery(id+"F0.imprint","INTERSECT",VERTEX,{"derivedFrom":[subQ1,subQ3]});Q80=makeQuery(id+"F0.imprint","IMPRINT",FACE,{"disambiguationData":[TD([[makeQuery(id+"F0.imprint","IMPRINT",EDGE,{"disambiguationData":[TD([[subQ4,1.0]])],"derivedFrom":subQ3}),-1.0]])]});}
            var Q81;
            {var subQ0=sQuery(id+"F0.wireOp",EDGE,"E0.2.10");var subQ1=sQuery(id+"F0.wireOp",EDGE,"E0.2.1");var subQ2=makeQuery(id+"F0.imprint","INTERSECT",VERTEX,{"derivedFrom":[subQ1,subQ0]});Q81=makeQuery(id+"F0.imprint","IMPRINT",FACE,{"disambiguationData":[TD([[makeQuery(id+"F0.imprint","IMPRINT",EDGE,{"disambiguationData":[TD([[subQ2,-1.0]])],"derivedFrom":subQ1}),-1.0]])]});}
            var Q82;
            {var subQ1=sQuery(id+"F0.wireOp",EDGE,"E0.2.6");var subQ3=sQuery(id+"F0.wireOp",EDGE,"E0.2.12");var subQ4=makeQuery(id+"F0.imprint","INTERSECT",VERTEX,{"derivedFrom":[subQ1,subQ3]});Q82=makeQuery(id+"F0.imprint","IMPRINT",FACE,{"disambiguationData":[TD([[makeQuery(id+"F0.imprint","IMPRINT",EDGE,{"disambiguationData":[TD([[subQ4,-1.0]])],"derivedFrom":subQ3}),1.0]])]});}
            var Q83;
            {var subQ0=sQuery(id+"F0.wireOp",EDGE,"E0.1.20");var subQ1=sQuery(id+"F0.wireOp",EDGE,"E0.1.12");var subQ2=makeQuery(id+"F0.imprint","INTERSECT",VERTEX,{"derivedFrom":[subQ1,subQ0]});Q83=makeQuery(id+"F0.imprint","IMPRINT",FACE,{"disambiguationData":[TD([[makeQuery(id+"F0.imprint","IMPRINT",EDGE,{"disambiguationData":[TD([[subQ2,-1.0]])],"derivedFrom":subQ1}),1.0]])]});}
            var Q84;
            {var subQ0=sQuery(id+"F0.wireOp",EDGE,"E0.2.20");var subQ1=sQuery(id+"F0.wireOp",EDGE,"E0.2.12");var subQ2=makeQuery(id+"F0.imprint","INTERSECT",VERTEX,{"derivedFrom":[subQ1,subQ0]});Q84=makeQuery(id+"F0.imprint","IMPRINT",FACE,{"disambiguationData":[TD([[makeQuery(id+"F0.imprint","IMPRINT",EDGE,{"disambiguationData":[TD([[subQ2,-1.0]])],"derivedFrom":subQ1}),1.0]])]});}
            var Q85;
            {var subQ1=sQuery(id+"F0.wireOp",EDGE,"E0.1.6");var subQ3=sQuery(id+"F0.wireOp",EDGE,"E0.1.12");var subQ4=makeQuery(id+"F0.imprint","INTERSECT",VERTEX,{"derivedFrom":[subQ1,subQ3]});Q85=makeQuery(id+"F0.imprint","IMPRINT",FACE,{"disambiguationData":[TD([[makeQuery(id+"F0.imprint","IMPRINT",EDGE,{"disambiguationData":[TD([[subQ4,-1.0]])],"derivedFrom":subQ3}),1.0]])]});}
            var Q86;
            Q86=makeQuery(id+"F0.imprint","IMPRINT",FACE,{"disambiguationData":[TD([[makeQuery(id+"F0.imprint","IMPRINT",EDGE,{"derivedFrom":sQuery(id+"F0.wireOp",EDGE,"E6")}),-1.0]])]});
            var Q87;
            Q87=makeQuery(id+"F0.imprint","IMPRINT",FACE,{"disambiguationData":[TD([[makeQuery(id+"F0.imprint","IMPRINT",EDGE,{"derivedFrom":sQuery(id+"F0.wireOp",EDGE,"E7.2.4")}),-1.0]])]});
            var Q88;
            {var subQ0=sQuery(id+"F0.wireOp",EDGE,"E7.2.1");var subQ1=sQuery(id+"F0.wireOp",EDGE,"E0.2.14");var subQ2=makeQuery(id+"F0.imprint","INTERSECT",VERTEX,{"derivedFrom":[subQ1,subQ0]});Q88=makeQuery(id+"F0.imprint","IMPRINT",FACE,{"disambiguationData":[TD([[makeQuery(id+"F0.imprint","IMPRINT",EDGE,{"disambiguationData":[TD([[subQ2,1.0]])],"derivedFrom":subQ1}),1.0]])]});}
            var Q89;
            {var subQ5=sQuery(id+"F0.wireOp",EDGE,"E0.2.14");var subQ8=makeQuery(id+"F0.imprint","INTERSECT",VERTEX,{"derivedFrom":[subQ5,sQuery(id+"F0.wireOp",EDGE,"E7.1.3")]});Q89=makeQuery(id+"F0.imprint","IMPRINT",FACE,{"disambiguationData":[TD([[makeQuery(id+"F0.imprint","IMPRINT",EDGE,{"disambiguationData":[TD([[subQ8,1.0]])],"derivedFrom":subQ5}),1.0]])]});}
            var Q90;
            {var subQ0=sQuery(id+"F0.wireOp",EDGE,"E7.1.2");var subQ1=sQuery(id+"F0.wireOp",EDGE,"E0.2.14");var subQ2=makeQuery(id+"F0.imprint","INTERSECT",VERTEX,{"derivedFrom":[subQ1,subQ0]});Q90=makeQuery(id+"F0.imprint","IMPRINT",FACE,{"disambiguationData":[TD([[makeQuery(id+"F0.imprint","IMPRINT",EDGE,{"disambiguationData":[TD([[subQ2,-1.0]])],"derivedFrom":subQ1}),1.0]])]});}
            var Q91;
            {var subQ0=sQuery(id+"F0.wireOp",EDGE,"E0.2.14");var subQ4=makeQuery(id+"F0.imprint","INTERSECT",VERTEX,{"derivedFrom":[subQ0,sQuery(id+"F0.wireOp",EDGE,"E2")]});Q91=makeQuery(id+"F0.imprint","IMPRINT",FACE,{"disambiguationData":[TD([[makeQuery(id+"F0.imprint","IMPRINT",EDGE,{"disambiguationData":[TD([[subQ4,1.0]])],"derivedFrom":subQ0}),1.0]])]});}
            var Q92;
            {var subQ0=sQuery(id+"F0.wireOp",EDGE,"E3.MirrorCS");var subQ1=sQuery(id+"F0.wireOp",EDGE,"E0.2.14");var subQ2=makeQuery(id+"F0.imprint","INTERSECT",VERTEX,{"derivedFrom":[subQ1,subQ0]});Q92=makeQuery(id+"F0.imprint","IMPRINT",FACE,{"disambiguationData":[TD([[makeQuery(id+"F0.imprint","IMPRINT",EDGE,{"disambiguationData":[TD([[subQ2,-1.0]])],"derivedFrom":subQ1}),1.0]])]});}
            var Q93;
            {var subQ5=sQuery(id+"F0.wireOp",EDGE,"E0.2.14");var subQ6=makeQuery(id+"F0.imprint","INTERSECT",VERTEX,{"derivedFrom":[subQ5,sQuery(id+"F0.wireOp",EDGE,"E7.2.3")]});Q93=makeQuery(id+"F0.imprint","IMPRINT",FACE,{"disambiguationData":[TD([[makeQuery(id+"F0.imprint","IMPRINT",EDGE,{"disambiguationData":[TD([[subQ6,1.0]])],"derivedFrom":subQ5}),1.0]])]});}
            var Q94;
            Q94=makeQuery(id+"F0.imprint","IMPRINT",FACE,{"disambiguationData":[TD([[makeQuery(id+"F0.imprint","IMPRINT",EDGE,{"derivedFrom":sQuery(id+"F0.wireOp",EDGE,"E7.1.4")}),-1.0]])]});
            var Q95;
            {var subQ5=sQuery(id+"F0.wireOp",EDGE,"E7.2.0");Q95=makeQuery(id+"F0.imprint","IMPRINT",FACE,{"disambiguationData":[TD([[makeQuery(id+"F0.imprint","IMPRINT",EDGE,{"derivedFrom":subQ5}),1.0]])]});}
            var Q96;
            {var subQ5=sQuery(id+"F0.wireOp",EDGE,"E7.1.0");Q96=makeQuery(id+"F0.imprint","IMPRINT",FACE,{"disambiguationData":[TD([[makeQuery(id+"F0.imprint","IMPRINT",EDGE,{"derivedFrom":subQ5}),1.0]])]});}
            extrude(context, id + "F1", {"entities" : qUnion([Q0, Q1, Q2, Q3, Q4, Q5, Q6, Q7, Q8, Q9, Q10, Q11, Q12, Q13, Q14, Q15, Q16, Q17, Q18, Q19, Q20, Q21, Q22, Q23, Q24, Q25, Q26, Q27, Q28, Q29, Q30, Q31, Q32, Q33, Q34, Q35, Q36, Q37, Q38, Q39, Q40, Q41, Q42, Q43, Q44, Q45, Q46, Q47, Q48, Q49, Q50, Q51, Q52, Q53, Q54, Q55, Q56, Q57, Q58, Q59, Q60, Q61, Q62, Q63, Q64, Q65, Q66, Q67, Q68, Q69, Q70, Q71, Q72, Q73, Q74, Q75, Q76, Q77, Q78, Q79, Q80, Q81, Q82, Q83, Q84, Q85, Q86, Q87, Q88, Q89, Q90, Q91, Q92, Q93, Q94, Q95, Q96]), "depth" : 7 * mm, "offsetDistance" : 25 * mm});
        }
        {
            var Q0;
            Q0=makeQuery(id+"F1.opExtrude","CAP_EDGE",EDGE,{"disambiguationData":[OSD([sQuery(id+"F0.wireOp",EDGE,"E5.1.0")])],"isStart":false});
            var Q1;
            Q1=makeQuery(id+"F1.opExtrude","CAP_EDGE",EDGE,{"disambiguationData":[OSD([sQuery(id+"F0.wireOp",EDGE,"E2")])],"isStart":false});
            var Q2;
            Q2=makeQuery(id+"F1.opExtrude","CAP_EDGE",EDGE,{"disambiguationData":[OSD([sQuery(id+"F0.wireOp",EDGE,"E1")])],"isStart":false});
            var Q3;
            Q3=makeQuery(id+"F1.opExtrude","CAP_EDGE",EDGE,{"disambiguationData":[OSD([sQuery(id+"F0.wireOp",EDGE,"E3.MirrorCS")])],"isStart":false});
            var Q4;
            Q4=makeQuery(id+"F1.opExtrude","CAP_EDGE",EDGE,{"disambiguationData":[OSD([sQuery(id+"F0.wireOp",EDGE,"E7.2.0")])],"isStart":false});
            var Q5;
            Q5=makeQuery(id+"F1.opExtrude","CAP_EDGE",EDGE,{"disambiguationData":[OSD([sQuery(id+"F0.wireOp",EDGE,"E7.2.1")])],"isStart":false});
            var Q6;
            Q6=makeQuery(id+"F1.opExtrude","CAP_EDGE",EDGE,{"disambiguationData":[OSD([sQuery(id+"F0.wireOp",EDGE,"E7.2.1")])],"isStart":true});
            var Q7;
            Q7=makeQuery(id+"F1.opExtrude","CAP_EDGE",EDGE,{"disambiguationData":[OSD([sQuery(id+"F0.wireOp",EDGE,"E7.2.0")])],"isStart":true});
            var Q8;
            Q8=makeQuery(id+"F1.opExtrude","CAP_EDGE",EDGE,{"disambiguationData":[OSD([sQuery(id+"F0.wireOp",EDGE,"E3.MirrorCS")])],"isStart":true});
            var Q9;
            Q9=makeQuery(id+"F1.opExtrude","CAP_EDGE",EDGE,{"disambiguationData":[OSD([sQuery(id+"F0.wireOp",EDGE,"E5.1.0")])],"isStart":true});
            var Q10;
            Q10=makeQuery(id+"F1.opExtrude","CAP_EDGE",EDGE,{"disambiguationData":[OSD([sQuery(id+"F0.wireOp",EDGE,"E7.1.2")])],"isStart":true});
            var Q11;
            Q11=makeQuery(id+"F1.opExtrude","CAP_EDGE",EDGE,{"disambiguationData":[OSD([sQuery(id+"F0.wireOp",EDGE,"E7.1.2")])],"isStart":false});
            var Q12;
            Q12=makeQuery(id+"F1.opExtrude","CAP_EDGE",EDGE,{"disambiguationData":[OSD([sQuery(id+"F0.wireOp",EDGE,"E7.1.1")])],"isStart":true});
            var Q13;
            Q13=makeQuery(id+"F1.opExtrude","CAP_EDGE",EDGE,{"disambiguationData":[OSD([sQuery(id+"F0.wireOp",EDGE,"E7.1.1")])],"isStart":false});
            var Q14;
            Q14=makeQuery(id+"F1.opExtrude","CAP_EDGE",EDGE,{"disambiguationData":[OSD([sQuery(id+"F0.wireOp",EDGE,"E7.1.0")])],"isStart":true});
            var Q15;
            Q15=makeQuery(id+"F1.opExtrude","CAP_EDGE",EDGE,{"disambiguationData":[OSD([sQuery(id+"F0.wireOp",EDGE,"E7.1.0")])],"isStart":false});
            var Q16;
            Q16=makeQuery(id+"F1.opExtrude","CAP_EDGE",EDGE,{"disambiguationData":[OSD([sQuery(id+"F0.wireOp",EDGE,"E1")])],"isStart":true});
            var Q17;
            Q17=makeQuery(id+"F1.opExtrude","CAP_EDGE",EDGE,{"disambiguationData":[OSD([sQuery(id+"F0.wireOp",EDGE,"E7.2.2")])],"isStart":false});
            var Q18;
            Q18=makeQuery(id+"F1.opExtrude","CAP_EDGE",EDGE,{"disambiguationData":[OSD([sQuery(id+"F0.wireOp",EDGE,"E7.2.2")])],"isStart":true});
            var Q19;
            Q19=makeQuery(id+"F1.opExtrude","CAP_EDGE",EDGE,{"disambiguationData":[OSD([sQuery(id+"F0.wireOp",EDGE,"E7.1.3")])],"isStart":false});
            var Q20;
            Q20=makeQuery(id+"F1.opExtrude","CAP_EDGE",EDGE,{"disambiguationData":[OSD([sQuery(id+"F0.wireOp",EDGE,"E7.1.3")])],"isStart":true});
            var Q21;
            Q21=makeQuery(id+"F1.opExtrude","CAP_EDGE",EDGE,{"disambiguationData":[OSD([sQuery(id+"F0.wireOp",EDGE,"E7.1.5")])],"isStart":true});
            var Q22;
            Q22=makeQuery(id+"F1.opExtrude","CAP_EDGE",EDGE,{"disambiguationData":[OSD([sQuery(id+"F0.wireOp",EDGE,"E7.2.3")])],"isStart":false});
            var Q23;
            Q23=makeQuery(id+"F1.opExtrude","CAP_EDGE",EDGE,{"disambiguationData":[OSD([sQuery(id+"F0.wireOp",EDGE,"E7.2.5")])],"isStart":false});
            var Q24;
            Q24=makeQuery(id+"F1.opExtrude","CAP_EDGE",EDGE,{"disambiguationData":[OSD([sQuery(id+"F0.wireOp",EDGE,"E7.2.3")])],"isStart":true});
            var Q25;
            Q25=makeQuery(id+"F1.opExtrude","CAP_EDGE",EDGE,{"disambiguationData":[OSD([sQuery(id+"F0.wireOp",EDGE,"E7.2.5")])],"isStart":true});
            var Q26;
            Q26=makeQuery(id+"F1.opExtrude","CAP_EDGE",EDGE,{"disambiguationData":[OSD([sQuery(id+"F0.wireOp",EDGE,"E4.1.3")])],"isStart":true});
            var Q27;
            Q27=makeQuery(id+"F1.opExtrude","CAP_EDGE",EDGE,{"disambiguationData":[OSD([sQuery(id+"F0.wireOp",EDGE,"E2")])],"isStart":true});
            var Q28;
            Q28=makeQuery(id+"F1.opExtrude","CAP_EDGE",EDGE,{"disambiguationData":[OSD([sQuery(id+"F0.wireOp",EDGE,"E4.1.3")])],"isStart":false});
            var Q29;
            Q29=makeQuery(id+"F1.opExtrude","CAP_EDGE",EDGE,{"disambiguationData":[OSD([sQuery(id+"F0.wireOp",EDGE,"E7.1.5")])],"isStart":false});
            fillet(context, id + "F2", {"entities" : qUnion([Q0, Q1, Q2, Q3, Q4, Q5, Q6, Q7, Q8, Q9, Q10, Q11, Q12, Q13, Q14, Q15, Q16, Q17, Q18, Q19, Q20, Q21, Q22, Q23, Q24, Q25, Q26, Q27, Q28, Q29]), "radius" : 2 * mm, "tangentPropagation" : true, "allowEdgeOverflow" : false});
        }
    });
